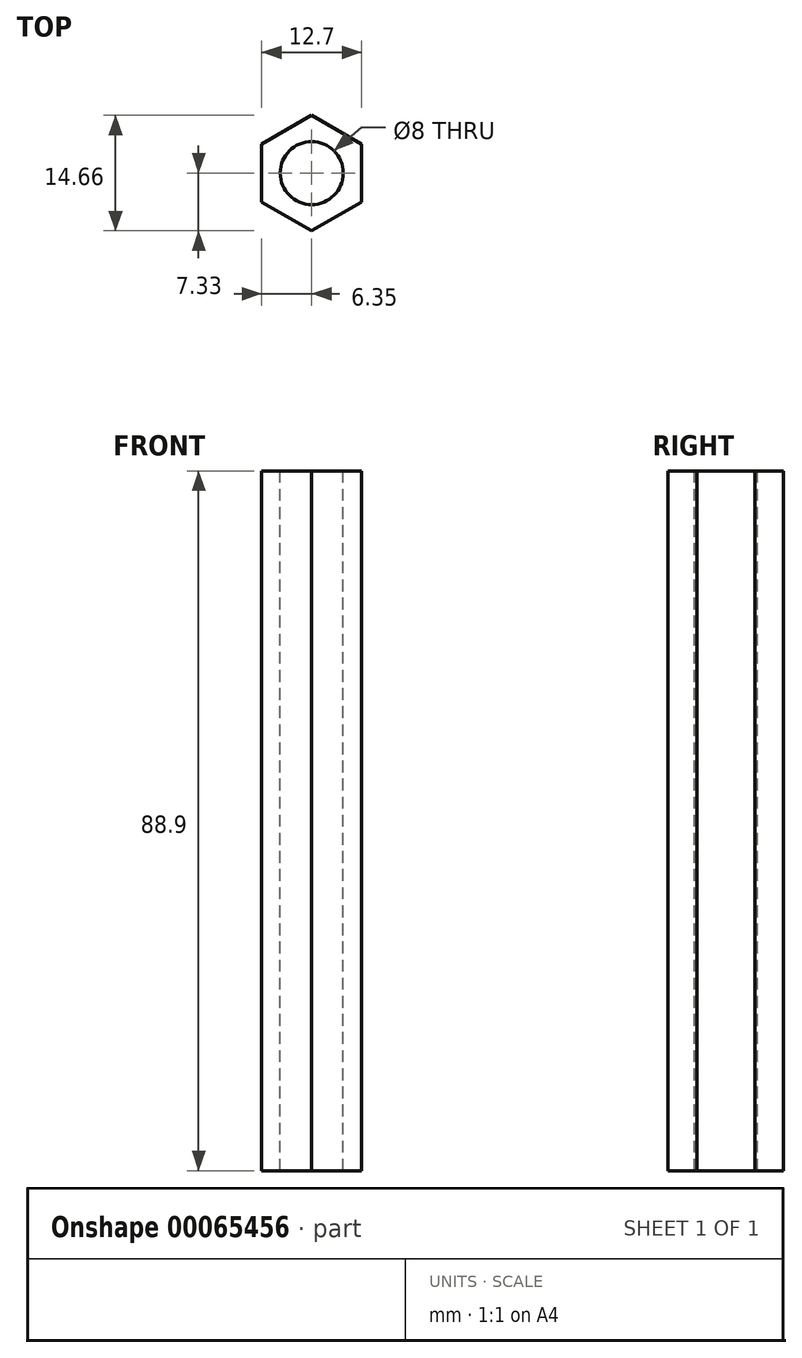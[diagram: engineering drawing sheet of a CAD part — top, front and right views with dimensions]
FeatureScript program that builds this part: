
annotation { "Feature Type Name" : "Feature", "Feature Type Description" : "" }
export const myFeature = defineFeature(function(context is Context, id is Id, definition is map)
    precondition{}
    {
        {
            var Q0;
            Q0=qCreatedBy(makeId("Top.planeOp"),FACE);
            var sketch = newSketch(context, id + "F0", { "sketchPlane" : qUnion([Q0])});
            skCircle(sketch, "E0.cCircle", {"center": v(0, 0) * mm, "radius": 6.35 * mm, "construction": true});
            skLineSegment(sketch, "E0.0", {"start": v(6.35, 3.67) * mm, "end": v(6.35, -3.67) * mm});
            skLineSegment(sketch, "E0.1", {"start": v(6.35, -3.67) * mm, "end": v(0, -7.33) * mm});
            skLineSegment(sketch, "E0.2", {"start": v(0, -7.33) * mm, "end": v(-6.35, -3.67) * mm});
            skLineSegment(sketch, "E0.3", {"start": v(-6.35, -3.67) * mm, "end": v(-6.35, 3.67) * mm});
            skLineSegment(sketch, "E0.4", {"start": v(-6.35, 3.67) * mm, "end": v(0, 7.33) * mm});
            skLineSegment(sketch, "E0.5", {"start": v(0, 7.33) * mm, "end": v(6.35, 3.67) * mm});
            skPoint(sketch, "E0.0.midPoint", {"position": v(6.35, 0) * mm});
            skSolve(sketch);
        }
        {
            var Q0;
            Q0=makeQuery(id+"F0.imprint","IMPRINT",FACE,{"disambiguationData":[TD([[makeQuery(id+"F0.imprint","IMPRINT",EDGE,{"derivedFrom":sQuery(id+"F0.wireOp",EDGE,"E0.0")}),-1.0]])]});
            extrude(context, id + "F1", {"entities" : qUnion([Q0]), "depth" : 88.9 * mm});
        }
        {
            var Q0;
            Q0=makeQuery(id+"F1.opExtrude","CAP_FACE",FACE,{"disambiguationData":[OSD([sQuery(id+"F0.wireOp",EDGE,"E0.0"),sQuery(id+"F0.wireOp",EDGE,"E0.1"),sQuery(id+"F0.wireOp",EDGE,"E0.2"),sQuery(id+"F0.wireOp",EDGE,"E0.3"),sQuery(id+"F0.wireOp",EDGE,"E0.4"),sQuery(id+"F0.wireOp",EDGE,"E0.5")])],"isStart":false});
            var sketch = newSketch(context, id + "F2", { "sketchPlane" : qUnion([Q0])});
            skCircle(sketch, "E1", {"center": v(0, 0) * mm, "radius": 4 * mm});
            skSolve(sketch);
        }
        {
            var Q0;
            Q0=sQuery(id+"F2.wireOp",VERTEX,"E1.center");
            var Q1;
            Q1=makeQuery(id+"F1.opExtrude","SWEPT_BODY",BODY,{"disambiguationData":[OSD([sQuery(id+"F0.wireOp",EDGE,"E0.0"),sQuery(id+"F0.wireOp",EDGE,"E0.1"),sQuery(id+"F0.wireOp",EDGE,"E0.2"),sQuery(id+"F0.wireOp",EDGE,"E0.3"),sQuery(id+"F0.wireOp",EDGE,"E0.4"),sQuery(id+"F0.wireOp",EDGE,"E0.5")])]});
            hole(context, id + "F3", {"style" : HoleStyle.SIMPLE, "holeDiameter" : 8 * mm, "endStyle" : HoleEndStyle.THROUGH, "locations" : qUnion([Q0]), "scope" : qUnion([Q1])});
        }
    });
